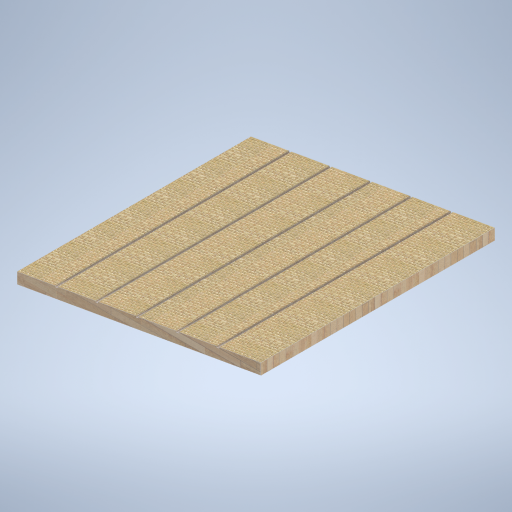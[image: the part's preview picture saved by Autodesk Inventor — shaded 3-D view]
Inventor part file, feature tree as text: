
AUTODESK INVENTOR PART (.ipt)
format: ipt  version: 2024.2 (Build 282272000, 272)  size: 424,448 bytes
history: native  units: mm
features: sketch x4, plane x3, extrude x2
ambient origin geometry x8: Origin, YZ Plane, XZ Plane, XY Plane, X Axis, Y Axis, Z Axis, Center Point
bodies: Solid1 (feature_tree)
feature tree (9):
  sketch  "Sketch1"  dims[d0=100.0mm d1=2110.0mm]
  plane  "Work Plane2"
  sketch  "Sketch2"  dims[d2=2200.0mm d3=13.962634mm]
  plane  "Work Plane3"
  extrude  "Extrusion1"  Depth=2110.0mm
  extrude  "Extrusion2"  Depth=2200.0mm
  plane  "Work Plane1"
  sketch  "Sketch3"  dims[d4=13.962634mm]
  sketch  "Sketch4"  dims[d5=2110.0mm d6=0.0mm d7=350.0mm d8=350.0mm d9=350.0mm d10=350.0mm d11=350.0mm d12=0.0mm d13=0.0mm]
